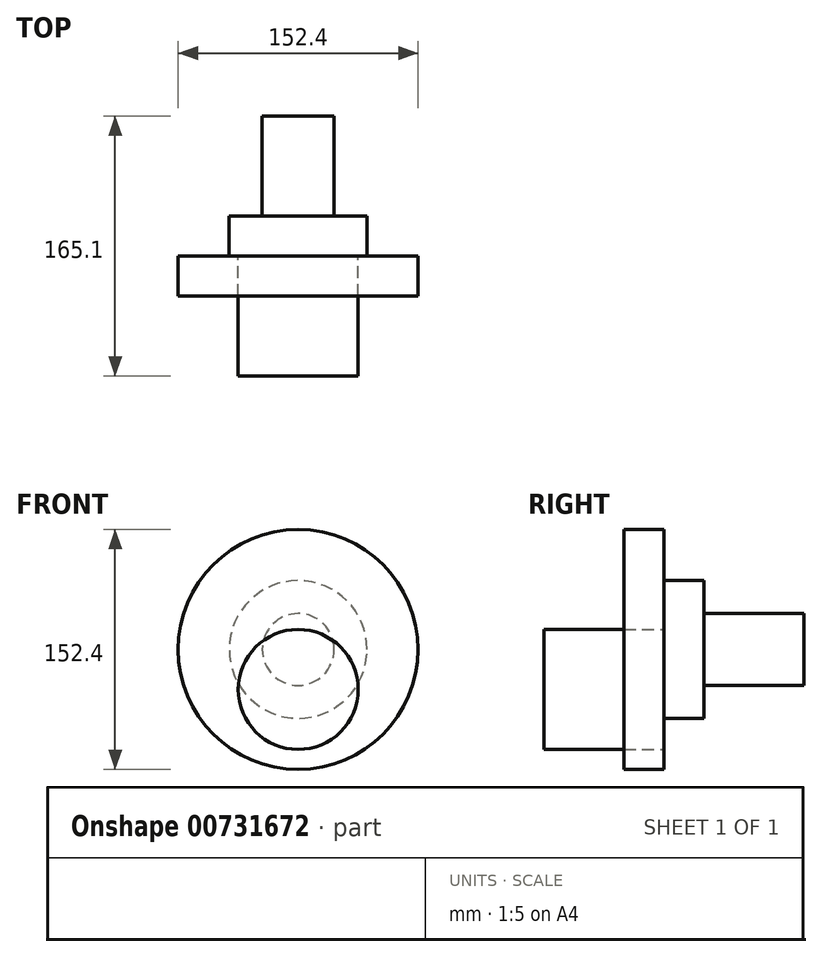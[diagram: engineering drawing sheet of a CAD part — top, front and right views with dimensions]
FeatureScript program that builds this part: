
annotation { "Feature Type Name" : "Feature", "Feature Type Description" : "" }
export const myFeature = defineFeature(function(context is Context, id is Id, definition is map)
    precondition{}
    {
        {
            var Q0;
            Q0=qCreatedBy(makeId("Front.planeOp"),FACE);
            var sketch = newSketch(context, id + "F0", { "sketchPlane" : qUnion([Q0])});
            skCircle(sketch, "E0", {"center": v(0, 0) * mm, "radius": 76.2 * mm});
            skSolve(sketch);
        }
        {
            var Q0;
            Q0=makeQuery(id+"F0.imprint","IMPRINT",FACE,{"disambiguationData":[TD([[makeQuery(id+"F0.imprint","IMPRINT",EDGE,{"derivedFrom":sQuery(id+"F0.wireOp",EDGE,"E0")}),1.0]])]});
            extrude(context, id + "F1", {"entities" : qUnion([Q0]), "depth" : 25.4 * mm, "offsetDistance" : 25.4 * mm});
        }
        {
            var Q0;
            Q0=qCreatedBy(makeId("Front.planeOp"),FACE);
            var sketch = newSketch(context, id + "F2", { "sketchPlane" : qUnion([Q0])});
            skCircle(sketch, "E1", {"center": v(0, -25.4) * mm, "radius": 38.1 * mm});
            skSolve(sketch);
        }
        {
            var Q0;
            Q0=makeQuery(id+"F2.imprint","IMPRINT",FACE,{"disambiguationData":[TD([[makeQuery(id+"F2.imprint","IMPRINT",EDGE,{"derivedFrom":sQuery(id+"F2.wireOp",EDGE,"E1")}),1.0]])]});
            var Q1;
            Q1=sQuery(id+"F2.wireOp",EDGE,"E1");
            extrude(context, id + "F3", {"entities" : qUnion([Q0]), "surfaceEntities" : qUnion([Q1]), "depth" : 76.2 * mm, "offsetDistance" : 25.4 * mm});
        }
        {
            var Q0;
            Q0=makeQuery(id+"F3.opExtrude","CAP_EDGE",EDGE,{"disambiguationData":[OSD([sQuery(id+"F2.wireOp",EDGE,"E1")])],"isStart":false});
            var Q1;
            Q1=makeQuery(id+"F1.opExtrude","CAP_EDGE",EDGE,{"disambiguationData":[OSD([sQuery(id+"F0.wireOp",EDGE,"E0")])],"isStart":false});
            loft(context, id + "F4", {"bodyType" : ToolBodyType.SURFACE, "wireProfilesArray" : [{ "wireProfileEntities" : qUnion([Q0]) }, { "wireProfileEntities" : qUnion([Q1]) }]});
        }
        {
            var Q0;
            Q0=makeQuery(id+"F1.opExtrude","CAP_FACE",FACE,{"disambiguationData":[OSD([sQuery(id+"F0.wireOp",EDGE,"E0")])],"isStart":true});
            var sketch = newSketch(context, id + "F5", { "sketchPlane" : qUnion([Q0])});
            skCircle(sketch, "E2", {"center": v(0, 0) * mm, "radius": 43.75 * mm});
            skSolve(sketch);
        }
        {
            var Q0;
            Q0=makeQuery(id+"F5.imprint","IMPRINT",FACE,{"disambiguationData":[TD([[makeQuery(id+"F5.imprint","IMPRINT",EDGE,{"derivedFrom":sQuery(id+"F5.wireOp",EDGE,"E2")}),1.0]])]});
            var Q1;
            Q1 = qBodyType(qCreatedBy(id + "F5" ,EDGE), BodyType.WIRE);
            var Q2;
            Q2=sQuery(id+"F5.wireOp",EDGE,"E2");
            extrude(context, id + "F6", {"entities" : qUnion([Q0]), "surfaceEntities" : qUnion([Q1, Q2]), "depth" : 25.4 * mm, "offsetDistance" : 25.4 * mm});
        }
        {
            var Q0;
            Q0=makeQuery(id+"F6.opExtrude","CAP_FACE",FACE,{"disambiguationData":[OSD([sQuery(id+"F5.wireOp",EDGE,"E2")])],"isStart":false});
            var sketch = newSketch(context, id + "F7", { "sketchPlane" : qUnion([Q0])});
            skCircle(sketch, "E3", {"center": v(0, 0) * mm, "radius": 22.82 * mm});
            skSolve(sketch);
        }
        {
            var Q0;
            Q0=makeQuery(id+"F7.imprint","IMPRINT",FACE,{"disambiguationData":[TD([[makeQuery(id+"F7.imprint","IMPRINT",EDGE,{"derivedFrom":sQuery(id+"F7.wireOp",EDGE,"E3")}),1.0]])]});
            var Q1;
            Q1=sQuery(id+"F7.wireOp",EDGE,"E3");
            extrude(context, id + "F8", {"entities" : qUnion([Q0]), "surfaceEntities" : qUnion([Q1]), "depth" : 63.5 * mm, "offsetDistance" : 25.4 * mm});
        }
        {
            var Q0;
            Q0=makeQuery(id+"F8.opExtrude","CAP_EDGE",EDGE,{"disambiguationData":[OSD([sQuery(id+"F7.wireOp",EDGE,"E3")])],"isStart":false});
            var Q1;
            Q1=makeQuery(id+"F6.opExtrude","CAP_EDGE",EDGE,{"disambiguationData":[OSD([sQuery(id+"F5.wireOp",EDGE,"E2")])],"isStart":false});
            var Q2;
            Q2=makeQuery(id+"F1.opExtrude","CAP_EDGE",EDGE,{"disambiguationData":[OSD([sQuery(id+"F0.wireOp",EDGE,"E0")])],"isStart":true});
            loft(context, id + "F9", {"bodyType" : ToolBodyType.SURFACE, "wireProfilesArray" : [{ "wireProfileEntities" : qUnion([Q0]) }, { "wireProfileEntities" : qUnion([Q1]) }, { "wireProfileEntities" : qUnion([Q2]) }]});
        }
    });
